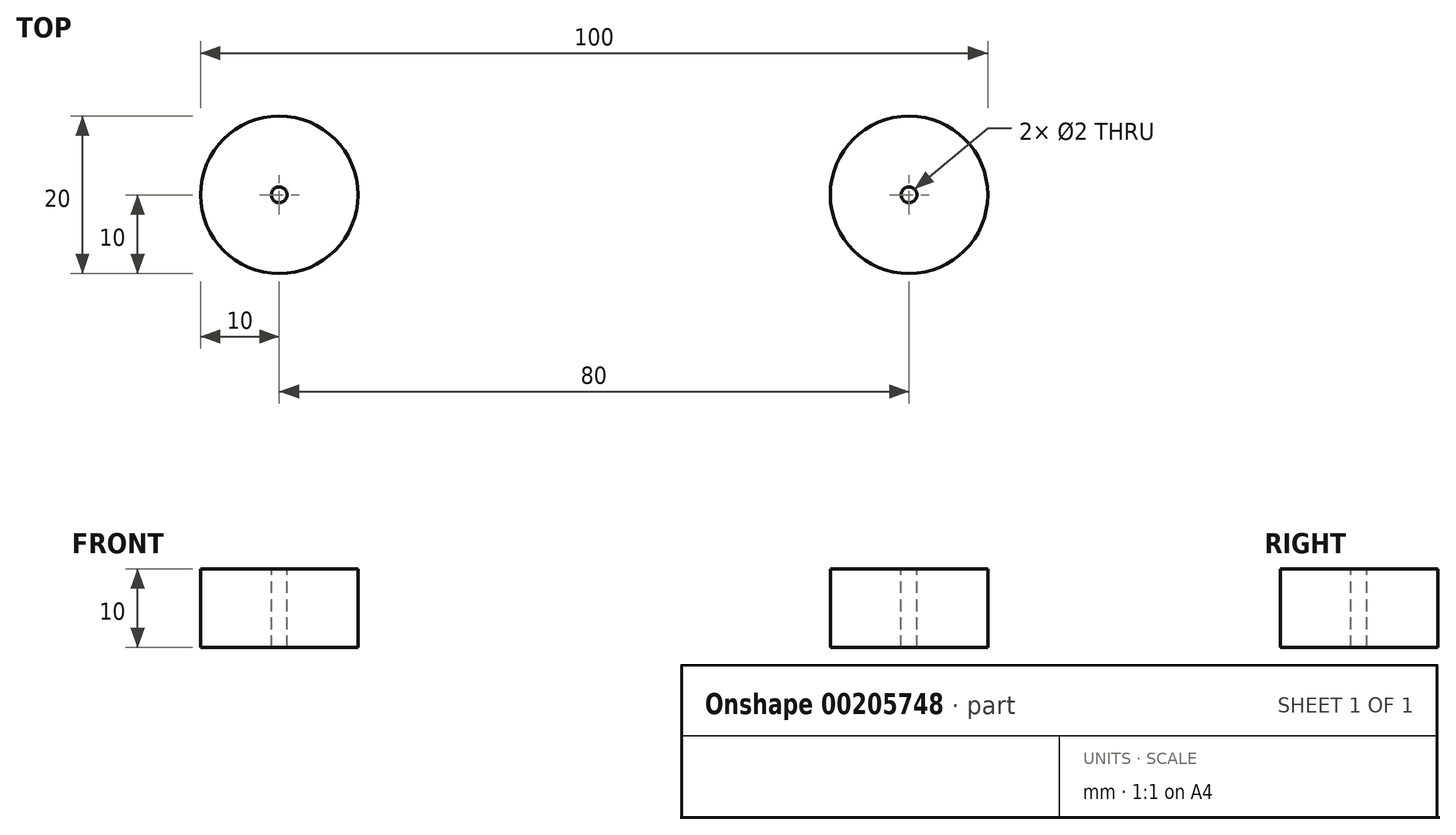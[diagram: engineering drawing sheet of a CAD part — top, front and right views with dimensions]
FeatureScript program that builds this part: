
annotation { "Feature Type Name" : "Feature", "Feature Type Description" : "" }
export const myFeature = defineFeature(function(context is Context, id is Id, definition is map)
    precondition{}
    {
        {
            var Q0;
            Q0=qCreatedBy(makeId("Top.planeOp"),FACE);
            var sketch = newSketch(context, id + "F0", { "sketchPlane" : qUnion([Q0])});
            skCircle(sketch, "E0", {"center": v(-40, 0) * mm, "radius": 10 * mm});
            skCircle(sketch, "E1.MirrorC", {"center": v(40, 0) * mm, "radius": 10 * mm});
            skCircle(sketch, "E2", {"center": v(-40, 0) * mm, "radius": 1 * mm});
            skCircle(sketch, "E3.MirrorC", {"center": v(40, 0) * mm, "radius": 1 * mm});
            skSolve(sketch);
        }
        {
            var Q0;
            Q0 = qSketchRegion(id + "F0", true);
            extrude(context, id + "F1", {"entities" : qUnion([Q0]), "oppositeDirection" : true, "depth" : 10 * mm});
        }
    });
